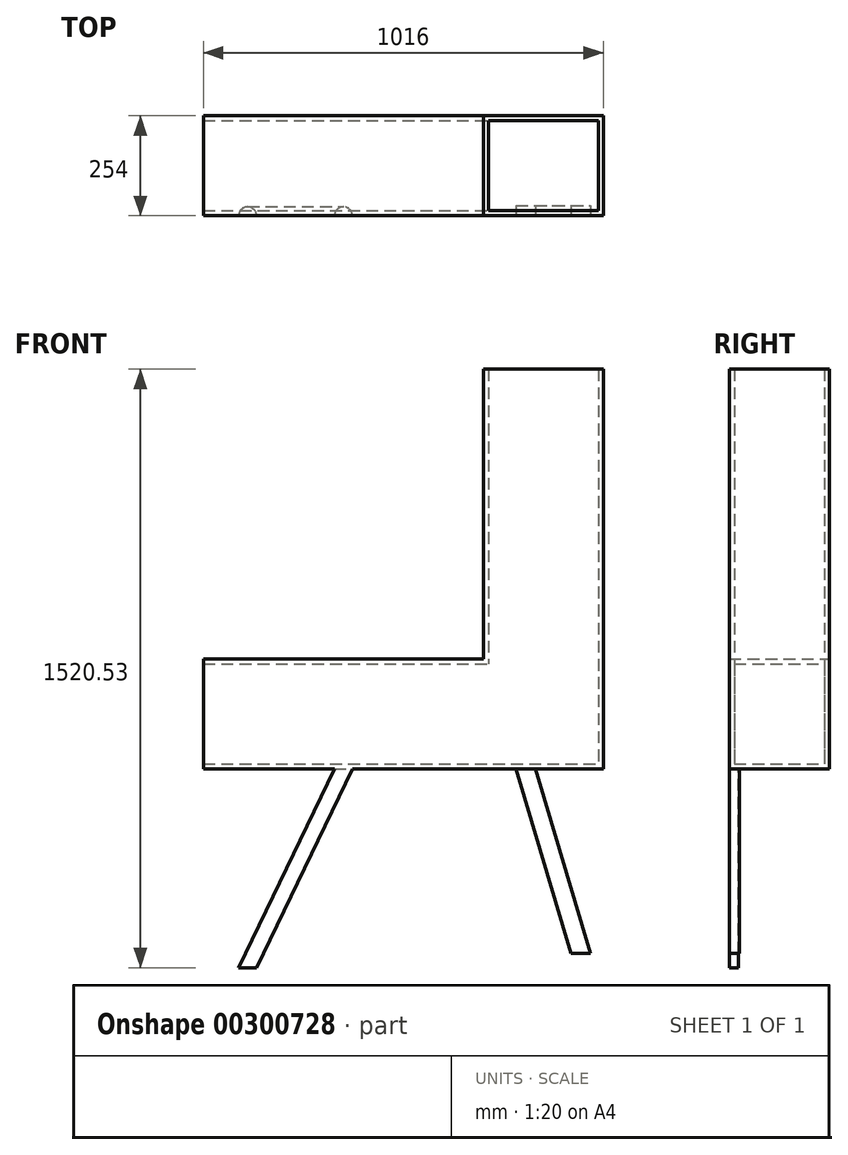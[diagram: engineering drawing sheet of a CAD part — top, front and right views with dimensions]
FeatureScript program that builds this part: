
annotation { "Feature Type Name" : "Feature", "Feature Type Description" : "" }
export const myFeature = defineFeature(function(context is Context, id is Id, definition is map)
    precondition{}
    {
        {
            var Q0;
            Q0=qCreatedBy(makeId("Front.planeOp"),FACE);
            var sketch = newSketch(context, id + "F0", { "sketchPlane" : qUnion([Q0])});
            skLineSegment(sketch, "E0", {"start": v(-608.8, -463.95) * mm, "end": v(407.2, -463.95) * mm});
            skLineSegment(sketch, "E1", {"start": v(407.2, 552.05) * mm, "end": v(407.2, -463.95) * mm});
            skLineSegment(sketch, "E2", {"start": v(-608.8, -463.95) * mm, "end": v(-608.8, -184.55) * mm});
            skLineSegment(sketch, "E3", {"start": v(-608.8, -184.55) * mm, "end": v(102.4, -184.55) * mm});
            skLineSegment(sketch, "E4", {"start": v(102.4, 552.05) * mm, "end": v(102.4, -184.55) * mm});
            skLineSegment(sketch, "E5", {"start": v(102.4, 552.05) * mm, "end": v(407.2, 552.05) * mm});
            skSolve(sketch);
        }
        {
            var Q0;
            Q0=makeQuery(id+"F0.imprint","IMPRINT",FACE,{"disambiguationData":[TD([[makeQuery(id+"F0.imprint","IMPRINT",EDGE,{"derivedFrom":sQuery(id+"F0.wireOp",EDGE,"E0")}),1.0]])]});
            extrude(context, id + "F1", {"entities" : qUnion([Q0]), "endBound" : BoundingType.SYMMETRIC, "depth" : 254 * mm});
        }
        {
            var Q0;
            Q0=makeQuery(id+"F1.opExtrude","SWEPT_FACE",FACE,{"disambiguationData":[OSD([sQuery(id+"F0.wireOp",EDGE,"E5")])]});
            shell(context, id + "F2", {"entities" : qUnion([Q0]), "thickness" : 12.7 * mm});
        }
        {
            var Q0;
            Q0=makeQuery(id+"F1.opExtrude","SWEPT_FACE",FACE,{"disambiguationData":[OSD([sQuery(id+"F0.wireOp",EDGE,"E2")])]});
            var sketch = newSketch(context, id + "F3", { "sketchPlane" : qUnion([Q0])});
            skLineSegment(sketch, "E6.bottom", {"start": v(114.3, -197.25) * mm, "end": v(-114.3, -197.25) * mm});
            skLineSegment(sketch, "E6.top", {"start": v(114.3, -451.25) * mm, "end": v(-114.3, -451.25) * mm});
            skLineSegment(sketch, "E6.left", {"start": v(114.3, -197.25) * mm, "end": v(114.3, -451.25) * mm});
            skLineSegment(sketch, "E6.right", {"start": v(-114.3, -197.25) * mm, "end": v(-114.3, -451.25) * mm});
            skPoint(sketch, "E6.middle", {"position": v(0, -324.25) * mm});
            skPoint(sketch, "E6.middle.positionSnap0", {"position": v(127, -324.25) * mm});
            skPoint(sketch, "E6.centerSnap0", {"position": v(127, -324.25) * mm});
            skSolve(sketch);
        }
        {
            var Q0;
            Q0=makeQuery(id+"F3.imprint","IMPRINT",FACE,{"disambiguationData":[TD([[makeQuery(id+"F3.imprint","IMPRINT",EDGE,{"derivedFrom":sQuery(id+"F3.wireOp",EDGE,"E6.bottom")}),1.0]])]});
            extrude(context, id + "F4", {"entities" : qUnion([Q0]), "operationType" : NewBodyOperationType.REMOVE, "oppositeDirection" : true, "depth" : 25.4 * mm});
        }
        {
            var Q0;
            Q0=makeQuery(id+"F1.opExtrude","CAP_FACE",FACE,{"disambiguationData":[OSD([sQuery(id+"F0.wireOp",EDGE,"E0"),sQuery(id+"F0.wireOp",EDGE,"E1"),sQuery(id+"F0.wireOp",EDGE,"E2"),sQuery(id+"F0.wireOp",EDGE,"E3"),sQuery(id+"F0.wireOp",EDGE,"E4"),sQuery(id+"F0.wireOp",EDGE,"E5")])],"isStart":false});
            var sketch = newSketch(context, id + "F5", { "sketchPlane" : qUnion([Q0])});
            skLineSegment(sketch, "E7", {"start": v(-244.68, -463.95) * mm, "end": v(-487.97, -968.48) * mm});
            skLineSegment(sketch, "E8", {"start": v(185.33, -463.95) * mm, "end": v(324.93, -932.41) * mm});
            skLineSegment(sketch, "E9", {"start": v(234.33, -463.95) * mm, "end": v(373.93, -932.41) * mm});
            skLineSegment(sketch, "E10", {"start": v(324.93, -932.41) * mm, "end": v(373.93, -932.41) * mm});
            skSolve(sketch);
        }
        {
            var Q0;
            Q0=makeQuery(id+"F1.opExtrude","SWEPT_FACE",FACE,{"disambiguationData":[OSD([sQuery(id+"F0.wireOp",EDGE,"E0")])]});
            var sketch = newSketch(context, id + "F6", { "sketchPlane" : qUnion([Q0])});
            skPoint(sketch, "E11.0", {"position": v(-253.2, 127) * mm});
            skCircle(sketch, "E12", {"center": v(-253.2, 127) * mm, "radius": 22.73 * mm});
            skSolve(sketch);
        }
        {
            var Q0;
            {var subQ0=sQuery(id+"F6.wireOp",EDGE,"E12");var subQ1=makeQuery(id+"F1.opExtrude","CAP_EDGE",EDGE,{"disambiguationData":[OSD([sQuery(id+"F0.wireOp",EDGE,"E0")])],"isStart":false});var subQ2=makeQuery(id+"F6.imprint","INTERSECT",VERTEX,{"disambiguationData":[OD(0.0)],"derivedFrom":[subQ1,subQ0]});Q0=makeQuery(id+"F6.imprint","IMPRINT",FACE,{"disambiguationData":[TD([[makeQuery(id+"F6.imprint","IMPRINT",EDGE,{"disambiguationData":[TD([[subQ2,-1.0]])],"derivedFrom":subQ0}),1.0]])]});}
            var Q1;
            Q1=sQuery(id+"F5.wireOp",EDGE,"E7");
            sweep(context, id + "F7", {"operationType" : NewBodyOperationType.ADD, "profiles" : qUnion([Q0]), "path" : qUnion([Q1])});
        }
        {
            var Q0;
            {var subQ0=sQuery(id+"F5.wireOp",EDGE,"E8");Q0=makeQuery(id+"F5.imprint","IMPRINT",FACE,{"disambiguationData":[TD([[makeQuery(id+"F5.imprint","IMPRINT",EDGE,{"derivedFrom":subQ0}),1.0]])]});}
            extrude(context, id + "F8", {"entities" : qUnion([Q0]), "oppositeDirection" : true, "depth" : 25.4 * mm});
        }
        {
            var Q0;
            Q0=makeQuery(id+"F1.opExtrude","SWEPT_FACE",FACE,{"disambiguationData":[OSD([sQuery(id+"F0.wireOp",EDGE,"E1")])]});
            cPlane(context, id + "F9", {"entities" : qUnion([Q0]), "cplaneType" : CPlaneType.OFFSET, "offset" : 203.2 * mm, "oppositeDirection" : true, "width" : 152.4 * mm, "height" : 152.4 * mm});
        }
        {
            var Q0;
            Q0=qCreatedBy(id+"F9.planeOp",FACE);
            var sketch = newSketch(context, id + "F10", { "sketchPlane" : qUnion([Q0])});
            skPoint(sketch, "E13.0", {"position": v(-127, -463.95) * mm});
            skLineSegment(sketch, "E14", {"start": v(-127, -463.95) * mm, "end": v(-474.17, -907.6) * mm});
            skLineSegment(sketch, "E15", {"start": v(-474.17, -907.6) * mm, "end": v(-415.2, -907.6) * mm});
            skLineSegment(sketch, "E16", {"start": v(-415.2, -907.6) * mm, "end": v(-68.02, -463.95) * mm});
            skLineSegment(sketch, "E17", {"start": v(-127, -463.95) * mm, "end": v(-68.02, -463.95) * mm});
            skLineSegment(sketch, "E18", {"start": v(-68.02, -463.95) * mm, "end": v(-127, -463.95) * mm});
            skSolve(sketch);
        }
        {
            var Q0;
            Q0=makeQuery(id+"F10.imprint","IMPRINT",FACE,{"disambiguationData":[TD([[makeQuery(id+"F10.imprint","IMPRINT",EDGE,{"derivedFrom":sQuery(id+"F10.wireOp",EDGE,"E14")}),1.0]])]});
            extrude(context, id + "F11", {"entities" : qUnion([Q0]), "endBound" : BoundingType.SYMMETRIC, "depth" : 76.2 * mm});
        }
        {
            var Q0;
            Q0=makeQuery(id+"F11.opExtrude","SWEPT_BODY",BODY,{"disambiguationData":[OSD([sQuery(id+"F10.wireOp",EDGE,"E14"),sQuery(id+"F10.wireOp",EDGE,"E15"),sQuery(id+"F10.wireOp",EDGE,"E16"),sQuery(id+"F10.wireOp",EDGE,"E18")])]});
            deleteBodies(context, id + "F12", {"entities" : qUnion([Q0])});
        }
    });
